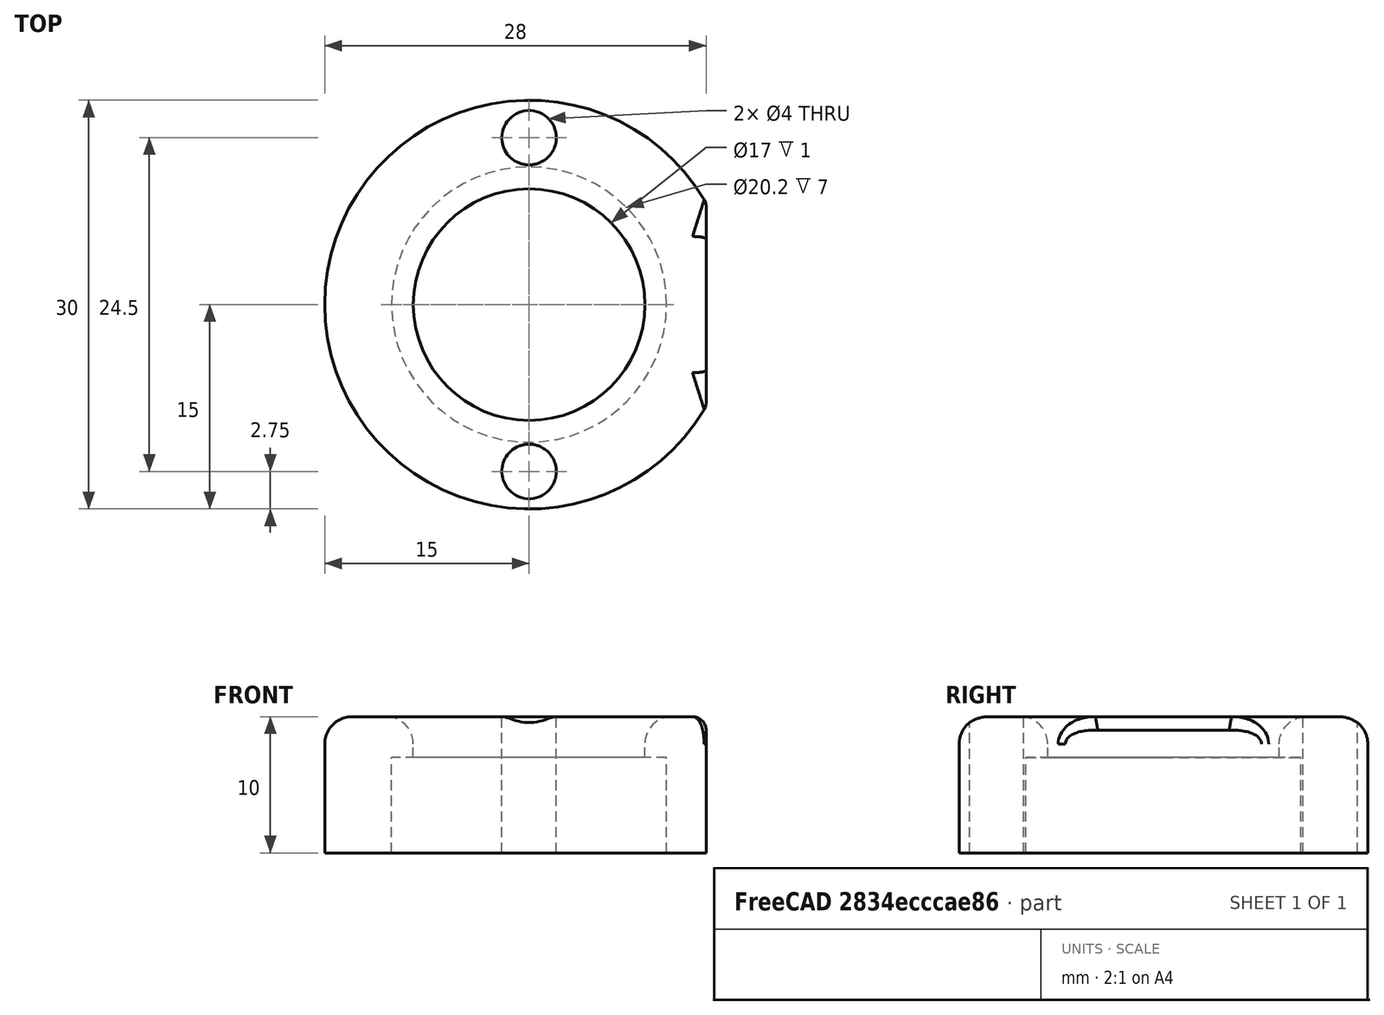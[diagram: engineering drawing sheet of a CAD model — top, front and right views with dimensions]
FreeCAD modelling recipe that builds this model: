
FCSTD DOCUMENT  (FreeCAD 0.18R16146 (Git))
Label: Skyddshylsa
License: All rights reserved
LicenseURL: http://en.wikipedia.org/wiki/All_rights_reserved
objects: Part::Cylinder×5, Part::Cut×3, Part::Fillet×3, Part::MultiFuse×2, Part::Box×1
note: 14 computed .brp shape members not serialized (recipe doc carries the construction recipe); baked Part::Feature solids carry a one-line shape summary decoded from their .brp

FEATURE [Part::Cylinder] Cylinder002  label="Hylsa"
  Angle = 360
  AttacherType = Attacher::AttachEngine3D
  Height = 10
  Radius = 15
FEATURE [Part::Cylinder] Cylinder004
  Angle = 360
  AttacherType = Attacher::AttachEngine3D
  Height = 3
  Radius = 8.5
FEATURE [Part::Cylinder] Cylinder005
  Angle = 360
  AttacherType = Attacher::AttachEngine3D
  Height = 10
  Placement = pos=(0,0,-10) rot=(0,0,1;0rad)
  Radius = 10.1
FEATURE [Part::MultiFuse] Fusion001
  Placement = pos=(0,0,7) rot=(0,0,1;0rad)
  Shapes = -> [Cylinder005,Cylinder004]
FEATURE [Part::Cut] Cut
  Base = -> Cylinder002
  Tool = -> Fusion001
FEATURE [Part::Fillet] Fillet
  Base = -> Cut
  Edges = 1 edges r=2: [Edge4]
FEATURE [Part::Fillet] Fillet001
  Base = -> Fillet
  Edges = 1 edges r=2: [Edge2]
FEATURE [Part::Box] Box  label="Cube"
  AttacherType = Attacher::AttachEngine3D
  Height = 10
  Length = 4
  Placement = pos=(13,-10,0) rot=(0,0,1;0rad)
  Width = 20
FEATURE [Part::Cut] Cut002
  Base = -> Fillet001
  Tool = -> Box
FEATURE [Part::Fillet] Fillet004
  Base = -> Cut002
  Edges = 4 edges r=1: [Edge3,Edge5,Edge8,Edge10]
FEATURE [Part::Cylinder] Cylinder009
  Angle = 360
  AttacherType = Attacher::AttachEngine3D
  Height = 10
  Placement = pos=(0,-12.25,0) rot=(0,0,1;0rad)
  Radius = 2
FEATURE [Part::Cylinder] Cylinder010
  Angle = 360
  AttacherType = Attacher::AttachEngine3D
  Height = 10
  Placement = pos=(0,12.25,0) rot=(0,0,1;0rad)
  Radius = 2
FEATURE [Part::MultiFuse] Fusion003
  Shapes = -> [Cylinder010,Cylinder009]
FEATURE [Part::Cut] Cut005  label="Hylsa002"
  Base = -> Fillet004
  Tool = -> Fusion003
